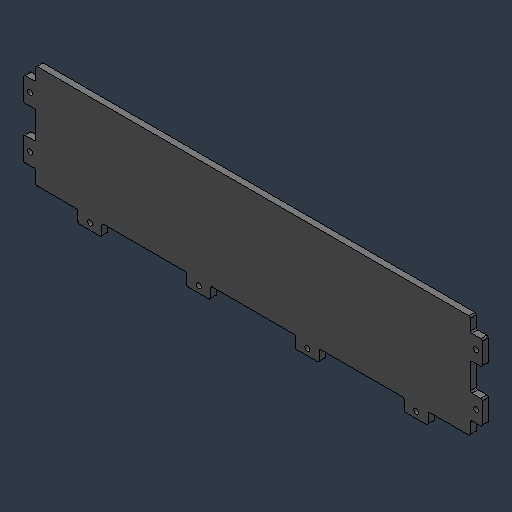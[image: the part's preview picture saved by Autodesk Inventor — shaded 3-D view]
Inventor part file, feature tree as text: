
AUTODESK INVENTOR PART (.ipt)
format: ipt  version: 2024.3 (Build 283343000, 343)  size: 138,240 bytes
history: native  units: mm (DEFAULTED — no unit token found)
features: mirror x1
ambient origin geometry x8: Origin, YZ Plane, XZ Plane, XY Plane, X Axis, Y Axis, Z Axis, Center Point
bodies: Solid1 (feature_tree)
feature tree (1):
  mirror  "Mirror2"
